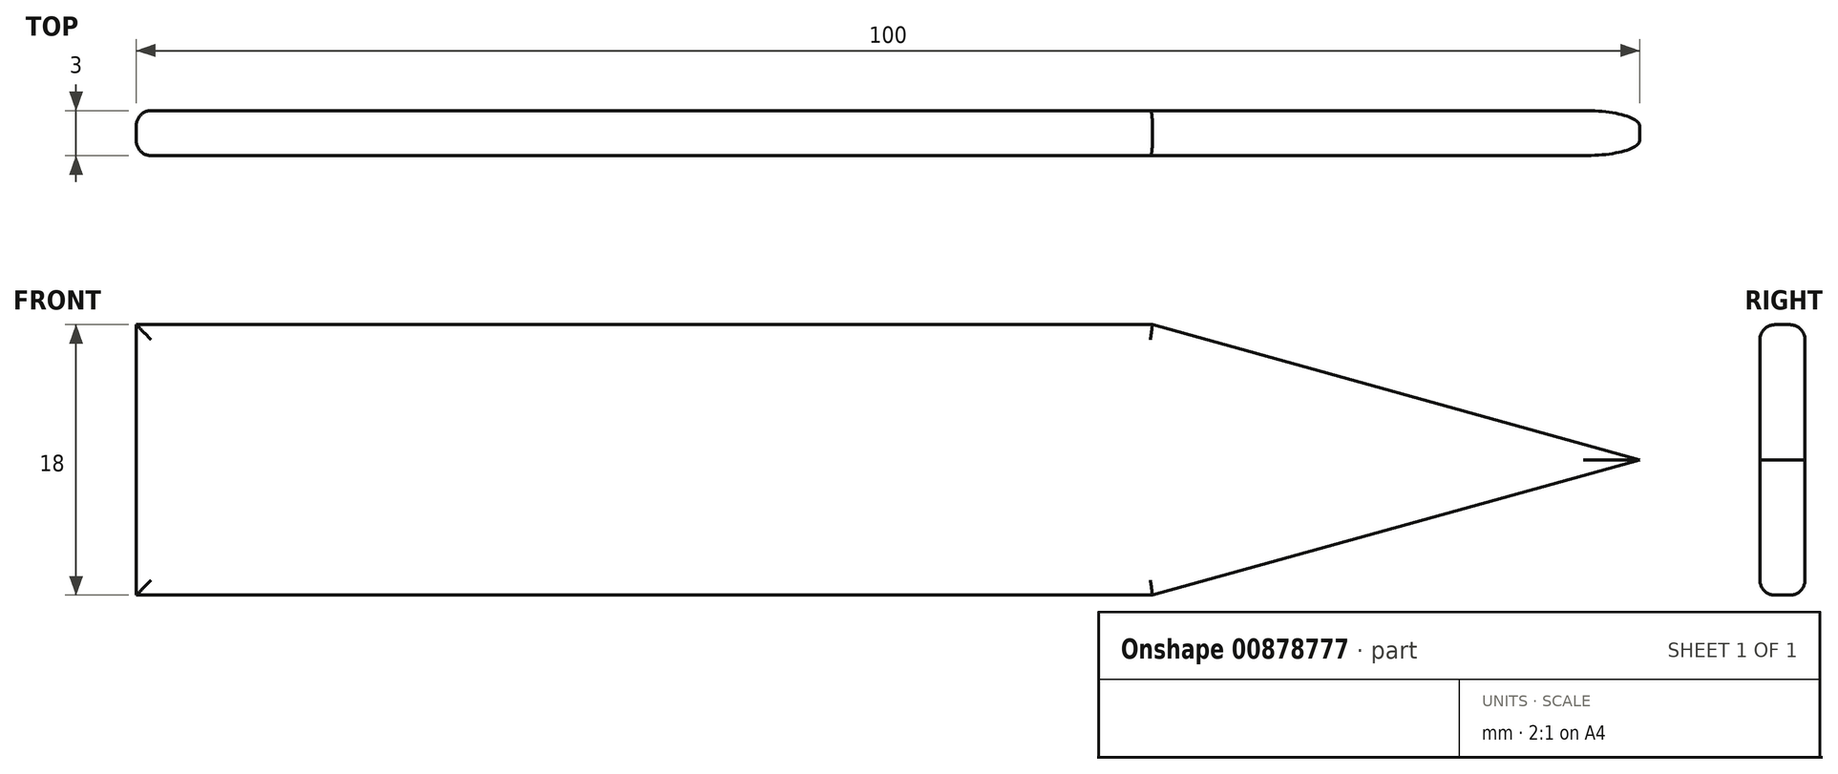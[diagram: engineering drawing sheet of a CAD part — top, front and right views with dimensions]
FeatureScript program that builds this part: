
annotation { "Feature Type Name" : "Feature", "Feature Type Description" : "" }
export const myFeature = defineFeature(function(context is Context, id is Id, definition is map)
    precondition{}
    {
        {
            var Q0;
            Q0=qCreatedBy(makeId("Front.planeOp"),FACE);
            var sketch = newSketch(context, id + "F0", { "sketchPlane" : qUnion([Q0])});
            skLineSegment(sketch, "E0", {"start": v(-12.43, 0) * mm, "end": v(75.62, 0) * mm});
            skLineSegment(sketch, "E1", {"start": v(75.62, 0) * mm, "end": v(43.21, -9) * mm});
            skLineSegment(sketch, "E2", {"start": v(43.21, -9) * mm, "end": v(-24.38, -9) * mm});
            skLineSegment(sketch, "E3", {"start": v(-24.38, -9) * mm, "end": v(-24.38, 9) * mm});
            skLineSegment(sketch, "E4", {"start": v(-24.38, 9) * mm, "end": v(43.21, 9) * mm});
            skLineSegment(sketch, "E5", {"start": v(43.21, 9) * mm, "end": v(75.62, 0) * mm});
            skLineSegment(sketch, "E6", {"start": v(-12.43, 0) * mm, "end": v(-24.38, 0) * mm});
            skSolve(sketch);
        }
        {
            var Q0;
            Q0=makeQuery(id+"F0.imprint","IMPRINT",FACE,{"disambiguationData":[TD([[makeQuery(id+"F0.imprint","IMPRINT",EDGE,{"derivedFrom":sQuery(id+"F0.wireOp",EDGE,"E0")}),1.0]])]});
            var Q1;
            Q1=makeQuery(id+"F0.imprint","IMPRINT",FACE,{"disambiguationData":[TD([[makeQuery(id+"F0.imprint","IMPRINT",EDGE,{"derivedFrom":sQuery(id+"F0.wireOp",EDGE,"E0")}),-1.0]])]});
            extrude(context, id + "F1", {"entities" : qUnion([Q0, Q1]), "depth" : 3 * mm, "offsetDistance" : 25.4 * mm});
        }
        {
            var Q0;
            Q0=makeQuery(id+"F1.opExtrude","CAP_FACE",FACE,{"disambiguationData":[OSD([sQuery(id+"F0.wireOp",EDGE,"E1"),sQuery(id+"F0.wireOp",EDGE,"E2"),sQuery(id+"F0.wireOp",EDGE,"E3"),sQuery(id+"F0.wireOp",EDGE,"E4"),sQuery(id+"F0.wireOp",EDGE,"E5")])],"isStart":false});
            var Q1;
            Q1=makeQuery(id+"F1.opExtrude","CAP_FACE",FACE,{"disambiguationData":[OSD([sQuery(id+"F0.wireOp",EDGE,"E1"),sQuery(id+"F0.wireOp",EDGE,"E2"),sQuery(id+"F0.wireOp",EDGE,"E3"),sQuery(id+"F0.wireOp",EDGE,"E4"),sQuery(id+"F0.wireOp",EDGE,"E5")])],"isStart":true});
            fillet(context, id + "F2", {"entities" : qUnion([Q0, Q1]), "radius" : 1 * mm, "tangentPropagation" : true, "allowEdgeOverflow" : false});
        }
    });
